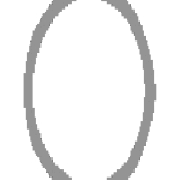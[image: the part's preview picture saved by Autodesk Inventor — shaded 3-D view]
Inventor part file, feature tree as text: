
AUTODESK INVENTOR PART (.ipt)
format: ipt  version: 2021 (Build 250183000, 183)  size: 111,104 bytes
history: native  units: in
note: dims shown in document units (in); Inventor stores cm internally (conversion verified against a paired STEP export)
features: other x4, sketch x3, plane x1
ambient origin geometry x8: Origin, YZ Plane, XZ Plane, XY Plane, X Axis, Y Axis, Z Axis, Center Point
bodies: Solid1 (feature_tree), Body (feature_tree)
feature tree (8):
  other  "Driven Length"
  other  "Frame Generator"
  other  "Start Plane"
  other  "End Plane"
  sketch  "Sketch"  dims[d2=39.5601in d4=-0.0in d5=39.5601in d6=0.12in d7=0.0in d8=90.0deg d9=39.5601in]
  sketch  "Sketch2"  dims[d0=1.0in]
  plane  "Work Plane3"
  sketch  "Sketch3"  dims[d1=0.065in]
